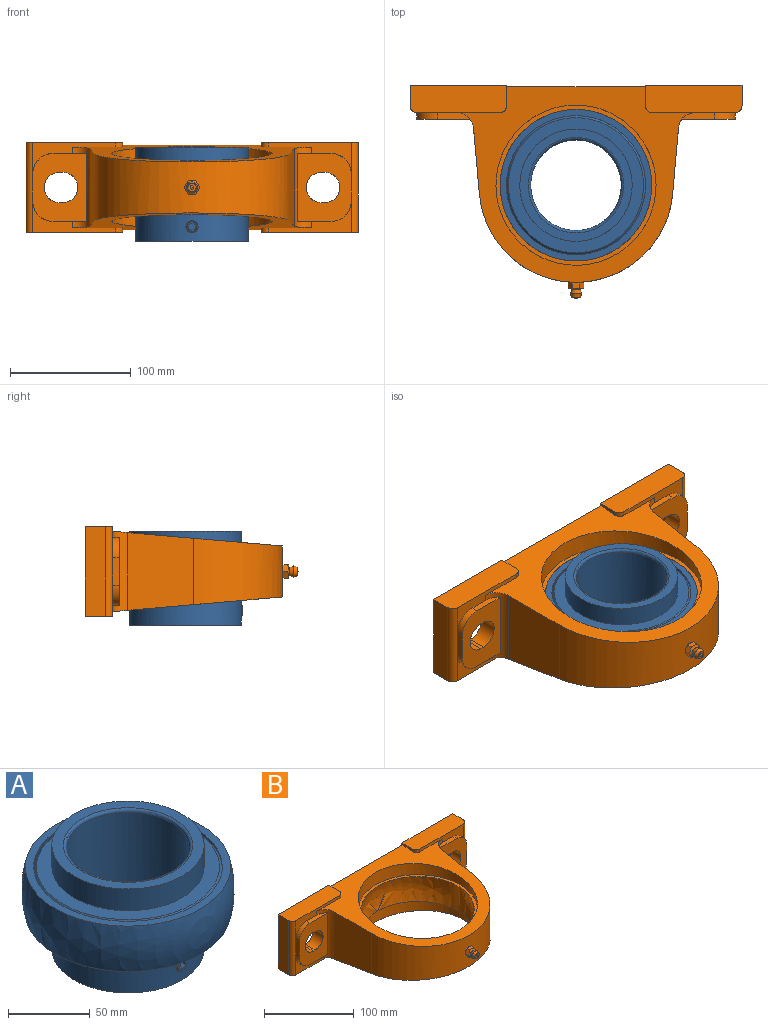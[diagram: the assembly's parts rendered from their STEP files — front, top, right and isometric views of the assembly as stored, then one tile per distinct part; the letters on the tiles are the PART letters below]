
ASSEMBLY  parts=2 mates=1
PART A: 143 faces, bbox 127.1x129.4x131.6 mm
  f0: plane 7.1x6.16mm, normal (0.87,0.5,0), area 38.5mm2, adj f1
  f1: cone r=1.71mm half-angle=45deg, axis (0.87,0.5,0), area 56.6mm2, adj f0,f2
  f2: cylinder r=5mm len=10.05mm, axis (0.87,0.5,0), area 79.3mm2, adj f1,f3
  f3: cylinder r=37.5mm len=75mm, axis (0,0,1), area 17220.6mm2, adj f2,f4,f139,f142
  f4: torus R=39.5mm, axis (0,0,-1), area 754.6mm2, adj f3,f5
  f5: plane 93.01x93.01mm, normal (0,0,-1), area 1887mm2, adj f4,f6
  f6: cylinder r=46.5mm len=93mm, axis (0,0,-1), area 7783.3mm2, adj f5,f7,f105,f106,f107,f108,f109,f110
  f7: sphere r=8.34mm, area 847.9mm2, adj f6,f8,f9,f10,f53,f54,f55,f56
  f8: torus R=51.49mm, axis (0,0,1), area 160.7mm2, adj f7,f9,f95,f106
  f9: torus R=51.49mm, axis (0,0,1), area 160.7mm2, adj f7,f8,f10,f106
  f10: cylinder r=56.49mm len=112.98mm, axis (0,0,1), area 2460.6mm2, adj f7,f9,f11,f13,f15,f17,f19,f21
  f11: torus R=51.49mm, axis (0,0,1), area 160.8mm2, adj f10,f12,f118,f120
  f12: torus R=51.49mm, axis (0,0,1), area 160.7mm2, adj f11,f95,f118,f120
  f13: torus R=51.49mm, axis (0,0,1), area 160.7mm2, adj f10,f14,f116,f118
  f14: torus R=51.49mm, axis (0,0,1), area 160.7mm2, adj f13,f95,f116,f118
  f15: torus R=51.49mm, axis (0,0,1), area 160.7mm2, adj f10,f16,f114,f116
  f16: torus R=51.49mm, axis (0,0,1), area 160.7mm2, adj f15,f95,f114,f116
  f17: torus R=51.49mm, axis (0,0,1), area 160.7mm2, adj f10,f18,f112,f114
  f18: torus R=51.49mm, axis (0,0,1), area 160.7mm2, adj f17,f95,f112,f114
  f19: torus R=51.49mm, axis (0,0,1), area 160.7mm2, adj f10,f20,f110,f112
  f20: torus R=51.49mm, axis (0,0,1), area 160.7mm2, adj f19,f95,f110,f112
  f21: torus R=51.49mm, axis (0,0,1), area 81.7mm2, adj f10,f22,f24,f110
  f22: torus R=51.49mm, axis (0,0,1), area 81.7mm2, adj f21,f23,f95,f110
  f23: torus R=51.49mm, axis (0,0,1), area 78.9mm2, adj f22,f24,f95,f108
  f24: torus R=51.49mm, axis (0,0,1), area 79mm2, adj f10,f21,f23,f108
  f25: torus R=51.49mm, axis (0,0,1), area 160.7mm2, adj f10,f26,f106,f108
  f26: torus R=51.49mm, axis (0,0,1), area 160.7mm2, adj f25,f95,f106,f108
  f27: torus R=51.49mm, axis (0,0,1), area 160.7mm2, adj f10,f28,f135,f137
  f28: torus R=51.49mm, axis (0,0,1), area 160.7mm2, adj f27,f95,f135,f137
  f29: torus R=51.49mm, axis (0,0,1), area 160.7mm2, adj f10,f30,f133,f135
  f30: torus R=51.49mm, axis (0,0,1), area 160.7mm2, adj f29,f95,f133,f135
  f31: torus R=51.49mm, axis (0,0,1), area 160.7mm2, adj f10,f32,f131,f133
  f32: torus R=51.49mm, axis (0,0,1), area 160.7mm2, adj f31,f95,f131,f133
  f33: torus R=51.49mm, axis (0,0,1), area 160.7mm2, adj f10,f34,f129,f131
  f34: torus R=51.49mm, axis (0,0,1), area 160.7mm2, adj f33,f95,f129,f131
  f35: torus R=51.49mm, axis (0,0,1), area 160.7mm2, adj f10,f36,f127,f129
  f36: torus R=51.49mm, axis (0,0,1), area 160.7mm2, adj f35,f95,f127,f129
  f37: torus R=51.49mm, axis (0,0,1), area 160.7mm2, adj f10,f38,f124,f127
  f38: torus R=51.49mm, axis (0,0,1), area 160.7mm2, adj f37,f95,f124,f127
  f39: torus R=51.49mm, axis (0,0,1), area 160.8mm2, adj f10,f40,f122,f124
  f40: torus R=51.49mm, axis (0,0,1), area 160.7mm2, adj f39,f95,f122,f124
  f41: torus R=51.49mm, axis (0,0,1), area 160.8mm2, adj f10,f42,f120,f122
  f42: torus R=51.49mm, axis (0,0,1), area 160.7mm2, adj f41,f95,f120,f122
  f43: cylinder r=0.87mm len=9.02mm, axis (0,-0.97,0.26), area 45.2mm2, adj f10,f44
  f44: sphere r=65mm, area 19597mm2, adj f43,f45
  f45: plane 125.48x125.48mm, normal (0,0,1), area 1907.7mm2, adj f44,f46
  f46: cylinder r=57.62mm len=115.24mm, axis (0,0,1), area 611.8mm2, adj f45,f47
  f47: cone r=55.93mm half-angle=45deg, axis (0,0,1), area 852.6mm2, adj f46,f48
  f48: plane 113.5x113.5mm, normal (0,0,1), area 3025.4mm2, adj f47,f49
  f49: cylinder r=46.51mm len=93.02mm, axis (0,0,-1), area 990.7mm2, adj f48,f50
  f50: plane 115.25x115.25mm, normal (0,0,-1), area 3627.1mm2, adj f49,f51
  f51: cylinder r=57.62mm len=115.24mm, axis (0,0,1), area 3.6mm2, adj f50,f52
  f52: plane 115.25x115.25mm, normal (0,0,1), area 412mm2, adj f10,f51
  f53: torus R=51.49mm, axis (0,0,1), area 160.7mm2, adj f7,f10,f54,f137
  f54: torus R=51.49mm, axis (0,0,1), area 160.7mm2, adj f7,f53,f95,f137
  f55: torus R=51.49mm, axis (0,0,1), area 120.6mm2, adj f7,f56,f137,f138
  f56: cylinder r=46.5mm len=93mm, axis (0,0,-1), area 10888.8mm2, adj f7,f55,f57,f67,f68,f69,f70,f71
  f57: cylinder r=5mm len=10mm, axis (-0.87,-0.5,0), area 4.9mm2, adj f56,f58
  f58: cone r=2.14mm half-angle=45deg, axis (-0.87,-0.5,0), area 37.1mm2, adj f57,f59
  f59: plane 8.28x7.19mm, normal (-0.87,-0.5,0), area 30.7mm2, adj f58,f60,f62,f63,f64,f65,f66
  f60: plane 5.58x4.67mm, normal (-0.25,0.43,0.87), area 14.4mm2, adj f59,f61,f62,f66
  f61: plane 5.77x4.33mm, normal (-0.87,-0.5,0), area 21.7mm2, adj f60,f62,f63,f64,f65,f66
  f62: plane 5.58x4.67mm, normal (0.25,-0.43,0.87), area 14.4mm2, adj f59,f60,f61,f63
  f63: plane 4.33x2.89mm, normal (0.5,-0.87,0), area 14.4mm2, adj f59,f61,f62,f64
  f64: plane 5.58x4.67mm, normal (0.25,-0.43,-0.87), area 14.4mm2, adj f59,f61,f63,f65
  f65: plane 5.58x4.67mm, normal (-0.25,0.43,-0.87), area 14.4mm2, adj f59,f61,f64,f66
  f66: plane 4.33x2.89mm, normal (-0.5,0.87,0), area 14.4mm2, adj f59,f60,f61,f65
  f67: torus R=51.49mm, axis (0,0,1), area 120.6mm2, adj f56,f118,f119,f120
  f68: torus R=51.49mm, axis (0,0,1), area 120.6mm2, adj f56,f116,f117,f118
  f69: torus R=51.49mm, axis (0,0,1), area 120.6mm2, adj f56,f114,f115,f116
  f70: torus R=51.49mm, axis (0,0,1), area 120.6mm2, adj f56,f112,f113,f114
  f71: torus R=51.49mm, axis (0,0,1), area 120.6mm2, adj f56,f110,f111,f112
  f72: torus R=51.49mm, axis (0,0,1), area 120.6mm2, adj f56,f108,f109,f110
  f73: torus R=51.49mm, axis (0,0,1), area 120.6mm2, adj f56,f106,f107,f108
  f74: torus R=51.49mm, axis (0,0,1), area 120.6mm2, adj f56,f135,f136,f137
  f75: torus R=51.49mm, axis (0,0,1), area 120.6mm2, adj f56,f133,f134,f135
  f76: torus R=51.49mm, axis (0,0,1), area 120.6mm2, adj f56,f131,f132,f133
  f77: torus R=51.49mm, axis (0,0,1), area 120.6mm2, adj f56,f129,f130,f131
  f78: torus R=51.49mm, axis (0,0,1), area 120.6mm2, adj f56,f127,f128,f129
  f79: torus R=51.49mm, axis (0,0,1), area 59.1mm2, adj f56,f80,f126,f127
  f80: torus R=51.49mm, axis (0,0,1), area 61.5mm2, adj f56,f79,f124,f125
  f81: torus R=51.49mm, axis (0,0,1), area 120.6mm2, adj f56,f122,f123,f124
  f82: torus R=51.49mm, axis (0,0,1), area 120.6mm2, adj f56,f120,f121,f122
  f83: plane 93.01x93.01mm, normal (0,0,1), area 1887mm2, adj f56,f142
  f84: cylinder r=5mm len=10mm, axis (0,1,0), area 4.9mm2, adj f56,f85
  f85: cone r=4.08mm half-angle=45deg, axis (0,1,0), area 37.1mm2, adj f84,f86
  f86: plane 8.28x8.28mm, normal (0,1,0), area 30.7mm2, adj f85,f87,f89,f90,f91,f92,f93
  f87: plane 5x2.5mm, normal (0.5,0,0.87), area 14.4mm2, adj f86,f88,f89,f93
  f88: plane 5.77x5mm, normal (0,1,0), area 21.7mm2, adj f87,f89,f90,f91,f92,f93
  f89: plane 5x2.5mm, normal (-0.5,0,0.87), area 14.4mm2, adj f86,f87,f88,f90
  f90: plane 5x2.89mm, normal (-1,0,0), area 14.4mm2, adj f86,f88,f89,f91
  f91: plane 5x2.5mm, normal (-0.5,0,-0.87), area 14.4mm2, adj f86,f88,f90,f92
  f92: plane 5x2.5mm, normal (0.5,0,-0.87), area 14.4mm2, adj f86,f88,f91,f93
  f93: plane 5x2.89mm, normal (1,0,0), area 14.4mm2, adj f86,f87,f88,f92
  f94: torus R=51.49mm, axis (0,0,1), area 120.6mm2, adj f7,f56,f105,f106
  f95: cylinder r=56.49mm len=112.98mm, axis (0,0,1), area 2463.2mm2, adj f7,f8,f12,f14,f16,f18,f20,f22
  f96: plane 115.25x115.25mm, normal (0,0,-1), area 397.7mm2, adj f95,f97
  f97: cylinder r=57.62mm len=115.24mm, axis (0,0,1), area 3.6mm2, adj f96,f98
  f98: plane 116.6x116.6mm, normal (0,0,1), area 3638.6mm2, adj f97,f99
  f99: cylinder r=46.51mm len=93.02mm, axis (0,0,1), area 990.7mm2, adj f98,f100
  f100: plane 113.5x113.5mm, normal (0,0,-1), area 3025.4mm2, adj f99,f101
  f101: cone r=55.93mm half-angle=45deg, axis (0,0,-1), area 852.6mm2, adj f100,f102
  f102: cylinder r=57.62mm len=115.24mm, axis (0,0,1), area 611.8mm2, adj f101,f103
  f103: plane 125.48x125.48mm, normal (0,0,-1), area 1909mm2, adj f102,f104
  f104: sphere r=65mm, area 19599.5mm2, adj f103
  f105: torus R=51.49mm, axis (0,0,1), area 120.6mm2, adj f6,f7,f94,f106
  f106: sphere r=8.34mm, area 847.9mm2, adj f6,f8,f9,f10,f25,f26,f56,f73
  f107: torus R=51.49mm, axis (0,0,1), area 120.6mm2, adj f6,f73,f106,f108
  f108: sphere r=8.34mm, area 847.9mm2, adj f6,f10,f23,f24,f25,f26,f56,f72
  f109: torus R=51.49mm, axis (0,0,1), area 120.6mm2, adj f6,f72,f108,f110
  f110: sphere r=8.34mm, area 847.9mm2, adj f6,f10,f19,f20,f21,f22,f56,f71
  f111: torus R=51.49mm, axis (0,0,1), area 120.6mm2, adj f6,f71,f110,f112
  f112: sphere r=8.34mm, area 847.9mm2, adj f6,f10,f17,f18,f19,f20,f56,f70
  f113: torus R=51.49mm, axis (0,0,1), area 120.6mm2, adj f6,f70,f112,f114
  f114: sphere r=8.34mm, area 847.9mm2, adj f6,f10,f15,f16,f17,f18,f56,f69
  f115: torus R=51.49mm, axis (0,0,1), area 120.6mm2, adj f6,f69,f114,f116
  f116: sphere r=8.34mm, area 847.9mm2, adj f6,f10,f13,f14,f15,f16,f56,f68
  f117: torus R=51.49mm, axis (0,0,1), area 120.6mm2, adj f6,f68,f116,f118
  f118: sphere r=8.34mm, area 847.9mm2, adj f6,f10,f11,f12,f13,f14,f56,f67
  f119: torus R=51.49mm, axis (0,0,1), area 120.6mm2, adj f6,f67,f118,f120
  f120: sphere r=8.34mm, area 847.9mm2, adj f6,f10,f11,f12,f41,f42,f56,f67
  f121: torus R=51.49mm, axis (0,0,1), area 120.6mm2, adj f6,f82,f120,f122
  f122: sphere r=8.34mm, area 847.9mm2, adj f6,f10,f39,f40,f41,f42,f56,f81
  f123: torus R=51.49mm, axis (0,0,1), area 120.6mm2, adj f6,f81,f122,f124
  f124: sphere r=8.34mm, area 847.9mm2, adj f6,f10,f37,f38,f39,f40,f56,f80
  f125: torus R=51.49mm, axis (0,0,1), area 61.5mm2, adj f6,f80,f124,f126
  f126: torus R=51.49mm, axis (0,0,1), area 59.1mm2, adj f6,f79,f125,f127
  f127: sphere r=8.34mm, area 847.9mm2, adj f6,f10,f35,f36,f37,f38,f56,f78
  f128: torus R=51.49mm, axis (0,0,1), area 120.6mm2, adj f6,f78,f127,f129
  f129: sphere r=8.34mm, area 847.9mm2, adj f6,f10,f33,f34,f35,f36,f56,f77
  f130: torus R=51.49mm, axis (0,0,1), area 120.6mm2, adj f6,f77,f129,f131
  f131: sphere r=8.34mm, area 847.9mm2, adj f6,f10,f31,f32,f33,f34,f56,f76
  f132: torus R=51.49mm, axis (0,0,1), area 120.6mm2, adj f6,f76,f131,f133
  f133: sphere r=8.34mm, area 847.9mm2, adj f6,f10,f29,f30,f31,f32,f56,f75
  f134: torus R=51.49mm, axis (0,0,1), area 120.6mm2, adj f6,f75,f133,f135
  f135: sphere r=8.34mm, area 847.9mm2, adj f6,f10,f27,f28,f29,f30,f56,f74
  f136: torus R=51.49mm, axis (0,0,1), area 120.6mm2, adj f6,f74,f135,f137
  f137: sphere r=8.34mm, area 847.9mm2, adj f6,f10,f27,f28,f53,f54,f55,f56
  f138: torus R=51.49mm, axis (0,0,1), area 120.6mm2, adj f6,f7,f55,f137
  f139: cylinder r=5mm len=10mm, axis (0,-1,0), area 79.3mm2, adj f3,f140
  f140: cone r=3.5mm half-angle=45deg, axis (0,-1,0), area 56.6mm2, adj f139,f141
  f141: plane 7.1x7.1mm, normal (0,-1,0), area 38.5mm2, adj f140
  f142: torus R=39.5mm, axis (0,0,-1), area 754.6mm2, adj f3,f83
PART B: 83 faces, bbox 315.1x216.6x170.1 mm
  f0: plane 65.39x49.89mm, normal (0,1,0), area 2651.8mm2, adj f8,f9,f10,f11,f13,f14,f15,f16
  f1: plane 65.39x49.89mm, normal (0,1,0), area 2651.8mm2, adj f3,f4,f5,f6,f18,f19,f20,f21
  f2: sphere r=65.01mm, area 12961.5mm2, adj f24,f27
  f3: plane 49.5x12.6mm, normal (1,0,0), area 623.7mm2, adj f1,f4,f6,f31
  f4: plane 65x12.6mm, normal (0,0,1), area 819mm2, adj f1,f3,f5,f31
  f5: plane 49.5x12.6mm, normal (-1,0,0), area 623.7mm2, adj f1,f4,f6,f31
  f6: plane 65x12.6mm, normal (0,0,-1), area 819mm2, adj f1,f3,f5,f31
  f7: plane 74x16.8mm, normal (1,0,0), area 1243.2mm2, adj f29,f30,f31,f32
  f8: plane 49.5x12.6mm, normal (1,0,0), area 623.7mm2, adj f0,f9,f11,f33
  f9: plane 65x12.6mm, normal (0,0,1), area 819mm2, adj f0,f8,f10,f33
  f10: plane 49.5x12.6mm, normal (-1,0,0), area 623.7mm2, adj f0,f9,f11,f33
  f11: plane 65x12.6mm, normal (0,0,-1), area 819mm2, adj f0,f8,f10,f33
  f12: plane 74x16.8mm, normal (-1,0,0), area 1243.2mm2, adj f33,f34,f35,f36
  f13: plane 15.4x3mm, normal (0,0,1), area 46.2mm2, adj f0,f14,f16,f39
  f14: cylinder r=12.5mm len=25mm, axis (0,-1,0), area 604.8mm2, adj f0,f13,f15,f39
  f15: plane 15.4x3mm, normal (0,0,-1), area 46.2mm2, adj f0,f14,f16,f39
  f16: cylinder r=12.5mm len=25mm, axis (0,-1,0), area 604.8mm2, adj f0,f13,f15,f39
  f17: plane 22.52x5.6mm, normal (-1,0,0), area 126.1mm2, adj f26,f36,f37,f39
  f18: plane 15.4x3mm, normal (0,0,1), area 46.2mm2, adj f1,f19,f21,f42
  f19: cylinder r=12.5mm len=25mm, axis (0,-1,0), area 604.8mm2, adj f1,f18,f20,f42
  f20: plane 15.4x3mm, normal (0,0,-1), area 46.2mm2, adj f1,f19,f21,f42
  f21: cylinder r=12.5mm len=25mm, axis (0,-1,0), area 604.8mm2, adj f1,f18,f20,f42
  f22: plane 22.52x5.6mm, normal (1,0,0), area 126.1mm2, adj f25,f28,f29,f42
  f23: sphere r=2.11mm, area 8.9mm2, adj f44
  f24: plane 172.74x172.74mm, normal (0,0,-1), area 1506mm2, adj f2,f45,f46
  f25: cylinder r=16.89mm len=16.89mm, axis (0,1,0), area 148.6mm2, adj f22,f41,f42,f47
  f26: cylinder r=16.89mm len=16.89mm, axis (0,1,0), area 148.6mm2, adj f17,f39,f40,f48
  f27: plane 172.74x172.74mm, normal (0,0,1), area 1506mm2, adj f2,f51
  f28: cylinder r=16.89mm len=16.89mm, axis (0,1,0), area 148.6mm2, adj f22,f42,f43,f52
  f29: cylinder r=5.6mm len=74mm, axis (0,0,1), area 650.9mm2, adj f7,f22,f30,f32,f47,f52
  f30: plane 80.35x22.75mm, normal (0,0,1), area 1778.7mm2, adj f7,f29,f31,f52,f53,f54
  f31: plane 80x74mm, normal (0,1,0), area 2702.5mm2, adj f3,f4,f5,f6,f7,f30,f32,f54
  f32: plane 80.35x22.75mm, normal (0,0,-1), area 1778.5mm2, adj f7,f29,f31,f47,f50,f54
  f33: plane 80x74mm, normal (0,1,0), area 2702.5mm2, adj f8,f9,f10,f11,f12,f34,f35,f56
  f34: plane 80.35x22.75mm, normal (0,0,-1), area 1778.7mm2, adj f12,f33,f36,f48,f49,f56
  f35: plane 80.35x22.75mm, normal (0,0,1), area 1778.5mm2, adj f12,f33,f36,f56,f57,f58
  f36: cylinder r=5.6mm len=74mm, axis (0,0,1), area 650.9mm2, adj f12,f17,f34,f35,f48,f58
  f37: cylinder r=16.89mm len=16.89mm, axis (0,1,0), area 148.6mm2, adj f17,f38,f39,f58
  f38: plane 27.73x5.93mm, normal (0,0,1), area 134.6mm2, adj f37,f39,f58,f59
  f39: plane 56.3x44.3mm, normal (0,-1,0), area 1805.6mm2, adj f13,f14,f15,f16,f17,f26,f37,f38
  f40: plane 27.74x5.93mm, normal (0,0,-1), area 134.6mm2, adj f26,f39,f48,f59
  f41: plane 27.65x5.84mm, normal (0,0,-1), area 134.6mm2, adj f25,f42,f47,f61
  f42: plane 56.3x44.3mm, normal (0,-1,0), area 1805.6mm2, adj f18,f19,f20,f21,f22,f25,f28,f41
  f43: plane 27.65x5.84mm, normal (0,0,1), area 134.6mm2, adj f28,f42,f52,f61
  f44: plane 7.06x7.06mm, normal (0,-1,0), area 30.6mm2, adj f23,f62
  f45: cylinder r=66.31mm len=132.62mm, axis (0,0,1), area 3063mm2, adj f24,f46,f63
  f46: cylinder r=66.31mm len=132.62mm, axis (0,0,1), area 1706.5mm2, adj f24,f45,f63
  f47: plane 68.8x25.74mm, normal (0,-1,0), area 487.9mm2, adj f25,f29,f32,f41,f50,f61,f63
  f48: plane 68.8x25.74mm, normal (0,-1,0), area 487.9mm2, adj f26,f34,f36,f40,f49,f59,f63
  f49: cylinder r=5.6mm len=5.6mm, axis (0,0,1), area 30.8mm2, adj f34,f48,f56,f63
  f50: cylinder r=5.6mm len=5.6mm, axis (0,0,-1), area 30.8mm2, adj f32,f47,f54,f63
  f51: cylinder r=66.31mm len=132.62mm, axis (0,0,-1), area 4442.1mm2, adj f27,f65
  f52: plane 68.8x25.74mm, normal (0,-1,0), area 487.9mm2, adj f28,f29,f30,f43,f53,f61,f65
  f53: cylinder r=5.6mm len=5.6mm, axis (0,0,-1), area 30.8mm2, adj f30,f52,f54,f65
  f54: plane 74x16.8mm, normal (-1,0,0), area 164mm2, adj f30,f31,f32,f50,f53,f55,f63,f65
  f55: plane 115x70.18mm, normal (0,1,0), area 8070.8mm2, adj f54,f56,f63,f65
  f56: plane 74x16.8mm, normal (1,0,0), area 164mm2, adj f33,f34,f35,f49,f55,f57,f63,f65
  f57: cylinder r=5.6mm len=5.6mm, axis (0,0,1), area 30.8mm2, adj f35,f56,f58,f65
  f58: plane 68.8x25.74mm, normal (0,-1,0), area 487.9mm2, adj f35,f36,f37,f38,f57,f59,f65
  f59: cylinder r=14mm len=66.51mm, axis (0,0,-1), area 627.5mm2, adj f38,f39,f40,f48,f58,f60,f63,f65
  f60: plane 64.3x54.43mm, normal (-1,-0.09,0), area 3256.2mm2, adj f59,f63,f65,f67
  f61: cylinder r=14mm len=66.51mm, axis (0,0,-1), area 627.5mm2, adj f41,f42,f43,f47,f52,f63,f64,f65
  f62: cone r=4.62mm half-angle=20deg, axis (0,1,0), area 84.4mm2, adj f44,f66
  f63: plane 205.48x169.85mm, normal (0,-0.09,-1), area 8924.4mm2, adj f45,f46,f47,f48,f49,f50,f54,f55
  f64: plane 64.3x54.43mm, normal (1,-0.09,0), area 3256.2mm2, adj f61,f63,f65,f67
  f65: plane 205.48x169.85mm, normal (0,-0.09,1), area 8912mm2, adj f51,f52,f53,f54,f55,f56,f57,f58
  f66: cone r=4.62mm half-angle=15deg, axis (0,-1,0), area 95.9mm2, adj f62,f71
  f67: cylinder r=80.4mm len=160.19mm, axis (0,0,1), area 12121.7mm2, adj f60,f63,f64,f65,f74
  f68: plane 7.55x7.01mm, normal (0.87,0,-0.5), area 30.1mm2, adj f69,f71,f72,f77,f78
  f69: plane 8.41x7.01mm, normal (0,0,-1), area 30.1mm2, adj f68,f70,f71,f78,f79
  f70: plane 7.55x7.01mm, normal (-0.87,0,-0.5), area 30.1mm2, adj f69,f71,f73,f75,f79
  f71: cone r=3.66mm half-angle=60deg, axis (0,1,0), area 101mm2, adj f66,f68,f69,f70,f72,f73,f80
  f72: plane 7.55x7.01mm, normal (0.87,0,0.5), area 30.1mm2, adj f68,f71,f76,f77,f80
  f73: plane 7.55x7.01mm, normal (-0.87,0,0.5), area 30.1mm2, adj f70,f71,f75,f80,f82
  f74: cylinder r=3.98mm len=7.96mm, axis (0,1,0), area 1.5mm2, adj f67,f81
  f75: cone r=5.56mm half-angle=60deg, axis (0,-1,0), area 3mm2, adj f70,f73,f81
  f76: cone r=5.56mm half-angle=60deg, axis (0,-1,0), area 3mm2, adj f72,f80,f81
  f77: cone r=5.56mm half-angle=60deg, axis (0,-1,0), area 3mm2, adj f68,f72,f81
  f78: cone r=5.56mm half-angle=60deg, axis (0,-1,0), area 2.6mm2, adj f68,f69,f81
  f79: cone r=5.56mm half-angle=60deg, axis (0,-1,0), area 3mm2, adj f69,f70,f81
  f80: plane 8.41x7.01mm, normal (0,0,1), area 30.1mm2, adj f71,f72,f73,f76,f82
  f81: plane 11.3x11.3mm, normal (0,1,0), area 47.5mm2, adj f74,f75,f76,f77,f78,f79,f82
  f82: cone r=5.56mm half-angle=60deg, axis (0,-1,0), area 2.6mm2, adj f73,f80,f81
PLACE A t=(-174.7,183.64,36.1)mm
PLACE B t=(-174.7,183.64,36.1)mm
MATE fastened A.f121 <-> B.f45  axis (0,0,-1) through (-66.2,101.04,-8.4)mm
